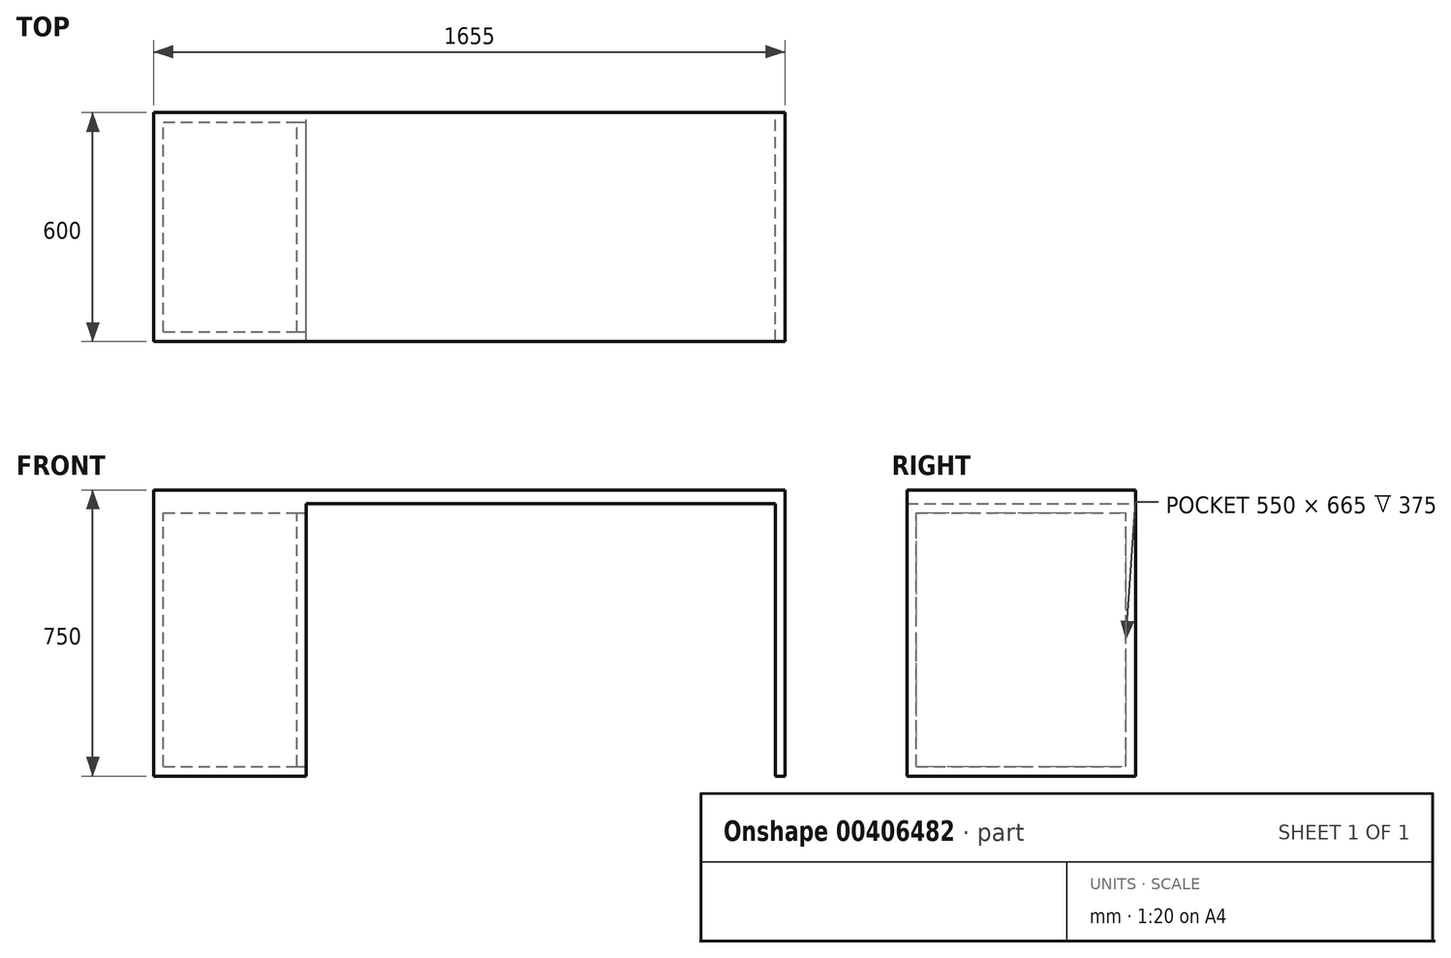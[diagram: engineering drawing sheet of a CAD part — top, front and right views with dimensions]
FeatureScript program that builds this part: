
annotation { "Feature Type Name" : "Feature", "Feature Type Description" : "" }
export const myFeature = defineFeature(function(context is Context, id is Id, definition is map)
    precondition{}
    {
        {
            var Q0;
            Q0=qCreatedBy(makeId("Front.planeOp"),FACE);
            var sketch = newSketch(context, id + "F0", { "sketchPlane" : qUnion([Q0])});
            skLineSegment(sketch, "E0.bottom", {"start": v(-827.5, 0) * mm, "end": v(-427.5, 0) * mm});
            skLineSegment(sketch, "E0.top", {"start": v(-827.5, 750) * mm, "end": v(-427.5, 750) * mm});
            skLineSegment(sketch, "E0.left", {"start": v(-827.5, 0) * mm, "end": v(-827.5, 750) * mm});
            skLineSegment(sketch, "E0.right", {"start": v(-427.5, 0) * mm, "end": v(-427.5, 750) * mm});
            skLineSegment(sketch, "E1.bottom", {"start": v(-427.5, 750) * mm, "end": v(827.5, 750) * mm});
            skLineSegment(sketch, "E1.top", {"start": v(-427.5, 715) * mm, "end": v(827.5, 715) * mm});
            skLineSegment(sketch, "E1.left", {"start": v(-427.5, 750) * mm, "end": v(-427.5, 715) * mm});
            skLineSegment(sketch, "E1.right", {"start": v(827.5, 750) * mm, "end": v(827.5, 715) * mm});
            skLineSegment(sketch, "E2.bottom", {"start": v(827.5, 715) * mm, "end": v(802.5, 715) * mm});
            skLineSegment(sketch, "E2.top", {"start": v(827.5, 0) * mm, "end": v(802.5, 0) * mm});
            skLineSegment(sketch, "E2.left", {"start": v(827.5, 715) * mm, "end": v(827.5, 0) * mm});
            skLineSegment(sketch, "E2.right", {"start": v(802.5, 715) * mm, "end": v(802.5, 0) * mm});
            skSolve(sketch);
        }
        {
            var Q0;
            Q0=qSketchRegion(id+"F0",true);
            extrude(context, id + "F1", {"entities" : qUnion([Q0]), "depth" : 600 * mm, "offsetDistance" : 25 * mm});
        }
        {
            var Q0;
            Q0=makeQuery(id+"F1.opExtrude","SWEPT_FACE",FACE,{"disambiguationData":[OSD([sQuery(id+"F0.wireOp",EDGE,"E0.right")])]});
            var sketch = newSketch(context, id + "F2", { "sketchPlane" : qUnion([Q0])});
            skLineSegment(sketch, "E3.bottom", {"start": v(-575, 25) * mm, "end": v(-25, 25) * mm});
            skLineSegment(sketch, "E3.top", {"start": v(-575, 690) * mm, "end": v(-25, 690) * mm});
            skLineSegment(sketch, "E3.left", {"start": v(-575, 25) * mm, "end": v(-575, 690) * mm});
            skLineSegment(sketch, "E3.right", {"start": v(-25, 25) * mm, "end": v(-25, 690) * mm});
            skSolve(sketch);
        }
        {
            var Q0;
            Q0=makeQuery(id+"F2.imprint","IMPRINT",FACE,{"disambiguationData":[TD([[makeQuery(id+"F2.imprint","IMPRINT",EDGE,{"derivedFrom":sQuery(id+"F2.wireOp",EDGE,"E3.bottom")}),1.0]])]});
            extrude(context, id + "F3", {"entities" : qUnion([Q0]), "operationType" : NewBodyOperationType.REMOVE, "endBound" : BoundingType.UP_TO_NEXT, "oppositeDirection" : true, "depth" : 25 * mm, "hasOffset" : true, "offsetDistance" : 25 * mm});
        }
        {
            var Q0;
            Q0=makeQuery(id+"F2.imprint","IMPRINT",FACE,{"disambiguationData":[TD([[makeQuery(id+"F2.imprint","IMPRINT",EDGE,{"derivedFrom":sQuery(id+"F2.wireOp",EDGE,"E3.bottom")}),1.0]])]});
            extrude(context, id + "F4", {"entities" : qUnion([Q0]), "oppositeDirection" : true, "depth" : 25 * mm, "offsetDistance" : 25 * mm});
        }
    });
